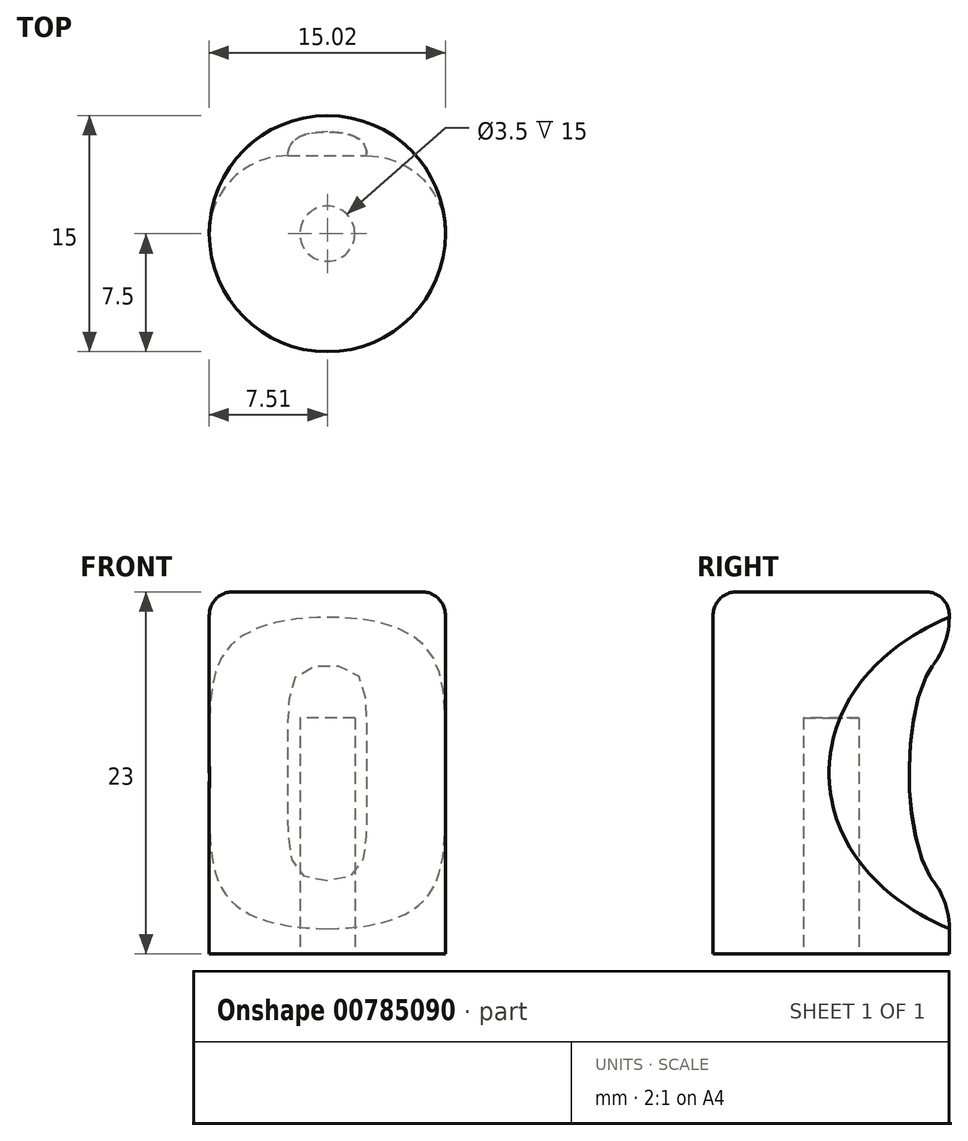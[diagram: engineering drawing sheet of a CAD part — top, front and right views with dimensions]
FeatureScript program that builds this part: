
annotation { "Feature Type Name" : "Feature", "Feature Type Description" : "" }
export const myFeature = defineFeature(function(context is Context, id is Id, definition is map)
    precondition{}
    {
        {
            var Q0;
            Q0=qCreatedBy(makeId("Top.planeOp"),FACE);
            var sketch = newSketch(context, id + "F0", { "sketchPlane" : qUnion([Q0])});
            skCircle(sketch, "E0", {"center": v(0, 0) * mm, "radius": 7.5 * mm});
            skCircle(sketch, "E1", {"center": v(0, 0) * mm, "radius": 1.75 * mm});
            skSolve(sketch);
        }
        {
            var Q0;
            Q0=makeQuery(id+"F0.imprint","IMPRINT",FACE,{"disambiguationData":[TD([[makeQuery(id+"F0.imprint","IMPRINT",EDGE,{"derivedFrom":sQuery(id+"F0.wireOp",EDGE,"E1")}),1.0]])]});
            var Q1;
            Q1=makeQuery(id+"F0.imprint","IMPRINT",FACE,{"disambiguationData":[TD([[makeQuery(id+"F0.imprint","IMPRINT",EDGE,{"derivedFrom":sQuery(id+"F0.wireOp",EDGE,"E0")}),1.0]])]});
            extrude(context, id + "F1", {"entities" : qUnion([Q0, Q1]), "depth" : 23 * mm, "offsetDistance" : 25 * mm});
        }
        {
            var Q0;
            Q0=makeQuery(id+"F0.imprint","IMPRINT",FACE,{"disambiguationData":[TD([[makeQuery(id+"F0.imprint","IMPRINT",EDGE,{"derivedFrom":sQuery(id+"F0.wireOp",EDGE,"E1")}),1.0]])]});
            extrude(context, id + "F2", {"entities" : qUnion([Q0]), "operationType" : NewBodyOperationType.REMOVE, "depth" : 15 * mm, "offsetDistance" : 25 * mm});
        }
        {
            var Q0;
            Q0=qCreatedBy(makeId("Right.planeOp"),FACE);
            var sketch = newSketch(context, id + "F3", { "sketchPlane" : qUnion([Q0])});
            skLineSegment(sketch, "E2", {"start": v(7.5, 23) * mm, "end": v(7.5, 0) * mm, "construction": true});
            skLineSegment(sketch, "E3", {"start": v(-7.5, 0) * mm, "end": v(-7.5, 23) * mm});
            skLineSegment(sketch, "E4", {"start": v(7.5, 19) * mm, "end": v(7.5, 4) * mm});
            skEllipse(sketch, "E5", {"center": v(7.5, 11.5) * mm, "majorRadius": 7.5 * mm, "minorRadius": 2.55 * mm, "majorAxis": v(0, -1)});
            skSolve(sketch);
        }
        {
            var Q0;
            {var subQ0=sQuery(id+"F3.wireOp",EDGE,"E4");Q0=makeQuery(id+"F3.imprint","IMPRINT",FACE,{"disambiguationData":[TD([[makeQuery(id+"F3.imprint","IMPRINT",EDGE,{"derivedFrom":subQ0}),-1.0]])]});}
            var Q1;
            Q1=sQuery(id+"F3.wireOp",EDGE,"E5");
            extrude(context, id + "F4", {"entities" : qUnion([Q0]), "operationType" : NewBodyOperationType.REMOVE, "surfaceEntities" : qUnion([Q1]), "endBound" : BoundingType.SYMMETRIC, "oppositeDirection" : true, "depth" : 15 * mm, "offsetDistance" : 25 * mm});
        }
        {
            var Q0;
            Q0=makeQuery(id+"F4.boolean.opBoolean","INTERSECT",EDGE,{"derivedFrom":[makeQuery(id+"F1.opExtrude","SWEPT_FACE",FACE,{"disambiguationData":[OSD([sQuery(id+"F0.wireOp",EDGE,"E0")])]}),makeQuery(id+"F4.opExtrude","SWEPT_FACE",FACE,{"disambiguationData":[OSD([sQuery(id+"F3.wireOp",EDGE,"E5")])]})]});
            fillet(context, id + "F5", {"entities" : qUnion([Q0]), "radius" : 5 * mm, "tangentPropagation" : true, "allowEdgeOverflow" : false});
        }
        {
            var Q0;
            Q0=makeQuery(id+"F1.opExtrude","CAP_EDGE",EDGE,{"disambiguationData":[OSD([sQuery(id+"F0.wireOp",EDGE,"E0")])],"isStart":false});
            fillet(context, id + "F6", {"entities" : qUnion([Q0]), "radius" : 1.5 * mm, "tangentPropagation" : true, "allowEdgeOverflow" : false});
        }
    });
